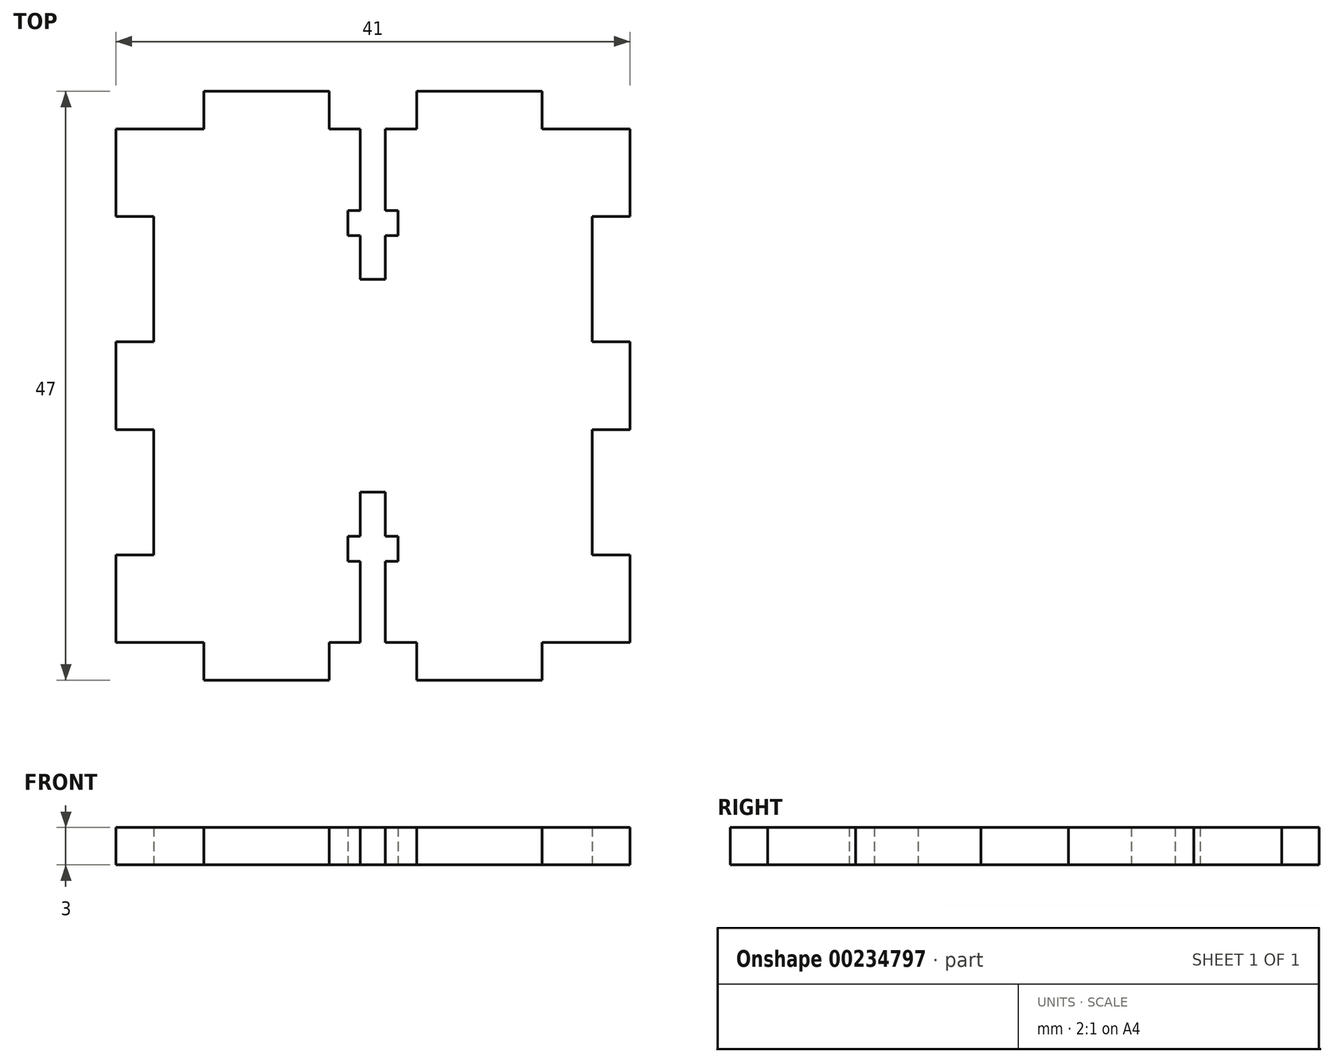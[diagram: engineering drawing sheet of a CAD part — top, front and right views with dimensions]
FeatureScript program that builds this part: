
annotation { "Feature Type Name" : "Feature", "Feature Type Description" : "" }
export const myFeature = defineFeature(function(context is Context, id is Id, definition is map)
    precondition{}
    {
        {
            var Q0;
            Q0=qCreatedBy(makeId("Top.planeOp"),FACE);
            var sketch = newSketch(context, id + "F0", { "sketchPlane" : qUnion([Q0])});
            skLineSegment(sketch, "E0.bottom", {"start": v(33.7, -13.23) * mm, "end": v(40.7, -13.23) * mm});
            skLineSegment(sketch, "E0.top", {"start": v(33.7, -54.23) * mm, "end": v(40.7, -54.23) * mm});
            skLineSegment(sketch, "E0.left", {"start": v(33.7, -13.23) * mm, "end": v(33.7, -20.23) * mm});
            skLineSegment(sketch, "E0.right", {"start": v(74.7, -13.23) * mm, "end": v(74.7, -20.23) * mm});
            skPoint(sketch, "E1", {"position": v(40.7, -13.23) * mm});
            skPoint(sketch, "E2", {"position": v(67.7, -13.23) * mm});
            skPoint(sketch, "E3", {"position": v(57.7, -13.23) * mm});
            skPoint(sketch, "E4", {"position": v(50.7, -13.23) * mm});
            skLineSegment(sketch, "E5", {"start": v(40.7, -13.23) * mm, "end": v(40.7, -10.23) * mm});
            skLineSegment(sketch, "E6", {"start": v(40.7, -10.23) * mm, "end": v(50.7, -10.23) * mm});
            skLineSegment(sketch, "E7", {"start": v(50.7, -10.23) * mm, "end": v(50.7, -13.23) * mm});
            skLineSegment(sketch, "E8", {"start": v(57.7, -13.23) * mm, "end": v(57.7, -10.23) * mm});
            skLineSegment(sketch, "E9", {"start": v(57.7, -10.23) * mm, "end": v(67.7, -10.23) * mm});
            skLineSegment(sketch, "E10", {"start": v(67.7, -10.23) * mm, "end": v(67.7, -13.23) * mm});
            skPoint(sketch, "E11", {"position": v(53.2, -13.23) * mm});
            skPoint(sketch, "E12", {"position": v(55.2, -13.23) * mm});
            skLineSegment(sketch, "E13", {"start": v(53.2, -13.23) * mm, "end": v(53.2, -19.73) * mm});
            skLineSegment(sketch, "E14", {"start": v(53.2, -19.73) * mm, "end": v(52.2, -19.73) * mm});
            skLineSegment(sketch, "E15", {"start": v(52.2, -19.73) * mm, "end": v(52.2, -21.73) * mm});
            skLineSegment(sketch, "E16", {"start": v(52.2, -21.73) * mm, "end": v(53.2, -21.73) * mm});
            skLineSegment(sketch, "E17", {"start": v(53.2, -21.73) * mm, "end": v(53.2, -25.23) * mm});
            skLineSegment(sketch, "E18", {"start": v(53.2, -25.23) * mm, "end": v(55.2, -25.23) * mm});
            skLineSegment(sketch, "E19", {"start": v(55.2, -25.23) * mm, "end": v(55.2, -21.73) * mm});
            skLineSegment(sketch, "E20", {"start": v(55.2, -21.73) * mm, "end": v(56.2, -21.73) * mm});
            skLineSegment(sketch, "E21", {"start": v(55.2, -19.73) * mm, "end": v(56.2, -19.73) * mm});
            skLineSegment(sketch, "E22", {"start": v(56.2, -19.73) * mm, "end": v(56.2, -21.73) * mm});
            skLineSegment(sketch, "E23.trimOffspring", {"start": v(55.2, -13.23) * mm, "end": v(57.7, -13.23) * mm});
            skLineSegment(sketch, "E24.trimOffspring", {"start": v(67.7, -13.23) * mm, "end": v(74.7, -13.23) * mm});
            skLineSegment(sketch, "E25.trimOffspring", {"start": v(50.7, -13.23) * mm, "end": v(53.2, -13.23) * mm});
            skLineSegment(sketch, "E26.MirrorCS", {"start": v(55.2, -45.73) * mm, "end": v(56.2, -45.73) * mm});
            skLineSegment(sketch, "E27.MirrorCS", {"start": v(52.2, -45.73) * mm, "end": v(53.2, -45.73) * mm});
            skLineSegment(sketch, "E28.MirrorCS", {"start": v(55.2, -47.73) * mm, "end": v(56.2, -47.73) * mm});
            skLineSegment(sketch, "E29.MirrorCS", {"start": v(56.2, -47.73) * mm, "end": v(56.2, -45.73) * mm});
            skLineSegment(sketch, "E30.MirrorCS", {"start": v(52.2, -47.73) * mm, "end": v(52.2, -45.73) * mm});
            skLineSegment(sketch, "E31.MirrorCS", {"start": v(53.2, -47.73) * mm, "end": v(52.2, -47.73) * mm});
            skLineSegment(sketch, "E32.MirrorCS", {"start": v(53.2, -42.23) * mm, "end": v(55.2, -42.23) * mm});
            skLineSegment(sketch, "E33.MirrorCS", {"start": v(55.2, -54.23) * mm, "end": v(57.7, -54.23) * mm});
            skLineSegment(sketch, "E34.MirrorCS", {"start": v(50.7, -57.23) * mm, "end": v(50.7, -54.23) * mm});
            skLineSegment(sketch, "E35.MirrorCS", {"start": v(57.7, -54.23) * mm, "end": v(57.7, -57.23) * mm});
            skLineSegment(sketch, "E36.MirrorCS", {"start": v(67.7, -57.23) * mm, "end": v(67.7, -54.23) * mm});
            skLineSegment(sketch, "E37.MirrorCS", {"start": v(50.7, -54.23) * mm, "end": v(53.2, -54.23) * mm});
            skLineSegment(sketch, "E38.MirrorCS", {"start": v(40.7, -54.23) * mm, "end": v(40.7, -57.23) * mm});
            skPoint(sketch, "E39.MirrorP", {"position": v(55.2, -54.23) * mm});
            skPoint(sketch, "E40.MirrorP", {"position": v(50.7, -54.23) * mm});
            skPoint(sketch, "E41.MirrorP", {"position": v(40.7, -54.23) * mm});
            skPoint(sketch, "E42.MirrorP", {"position": v(67.7, -54.23) * mm});
            skLineSegment(sketch, "E43.MirrorCS", {"start": v(57.7, -57.23) * mm, "end": v(67.7, -57.23) * mm});
            skPoint(sketch, "E44.MirrorP", {"position": v(57.7, -54.23) * mm});
            skLineSegment(sketch, "E45.MirrorCS", {"start": v(53.2, -54.23) * mm, "end": v(53.2, -47.73) * mm});
            skPoint(sketch, "E46.MirrorP", {"position": v(53.2, -54.23) * mm});
            skLineSegment(sketch, "E47.MirrorCS", {"start": v(67.7, -54.23) * mm, "end": v(74.7, -54.23) * mm});
            skLineSegment(sketch, "E48.MirrorCS", {"start": v(55.2, -42.23) * mm, "end": v(55.2, -45.73) * mm});
            skLineSegment(sketch, "E49.MirrorCS", {"start": v(53.2, -45.73) * mm, "end": v(53.2, -42.23) * mm});
            skLineSegment(sketch, "E50.MirrorCS", {"start": v(40.7, -57.23) * mm, "end": v(50.7, -57.23) * mm});
            skPoint(sketch, "E51", {"position": v(74.7, -20.23) * mm});
            skPoint(sketch, "E52", {"position": v(74.7, -47.23) * mm});
            skPoint(sketch, "E53", {"position": v(74.7, -33.73) * mm});
            skPoint(sketch, "E54", {"position": v(74.7, -30.23) * mm});
            skPoint(sketch, "E55", {"position": v(74.7, -37.23) * mm});
            skLineSegment(sketch, "E56.trimOffspring", {"start": v(74.7, -30.23) * mm, "end": v(74.7, -37.23) * mm});
            skLineSegment(sketch, "E57.trimOffspring", {"start": v(74.7, -47.23) * mm, "end": v(74.7, -54.23) * mm});
            skPoint(sketch, "E58.MirrorP", {"position": v(33.7, -37.23) * mm});
            skPoint(sketch, "E59.MirrorP", {"position": v(33.7, -47.23) * mm});
            skLineSegment(sketch, "E60.MirrorCS", {"start": v(33.7, -47.23) * mm, "end": v(33.7, -54.23) * mm});
            skPoint(sketch, "E61.MirrorP", {"position": v(33.7, -30.23) * mm});
            skPoint(sketch, "E62.MirrorP", {"position": v(33.7, -20.23) * mm});
            skPoint(sketch, "E63.MirrorP", {"position": v(33.7, -33.73) * mm});
            skLineSegment(sketch, "E64.MirrorCS", {"start": v(33.7, -30.23) * mm, "end": v(33.7, -37.23) * mm});
            skLineSegment(sketch, "E65", {"start": v(55.2, -13.23) * mm, "end": v(55.2, -19.73) * mm});
            skLineSegment(sketch, "E66", {"start": v(55.2, -54.23) * mm, "end": v(55.2, -47.73) * mm});
            skLineSegment(sketch, "E67", {"start": v(74.7, -37.23) * mm, "end": v(71.7, -37.23) * mm});
            skLineSegment(sketch, "E68", {"start": v(71.7, -37.23) * mm, "end": v(71.7, -47.23) * mm});
            skLineSegment(sketch, "E69", {"start": v(71.7, -47.23) * mm, "end": v(74.7, -47.23) * mm});
            skLineSegment(sketch, "E70", {"start": v(74.7, -30.23) * mm, "end": v(71.7, -30.23) * mm});
            skLineSegment(sketch, "E71", {"start": v(71.7, -30.23) * mm, "end": v(71.7, -20.23) * mm});
            skLineSegment(sketch, "E72", {"start": v(71.7, -20.23) * mm, "end": v(74.7, -20.23) * mm});
            skLineSegment(sketch, "E73", {"start": v(33.7, -37.23) * mm, "end": v(36.7, -37.23) * mm});
            skLineSegment(sketch, "E74", {"start": v(36.7, -37.23) * mm, "end": v(36.7, -47.23) * mm});
            skLineSegment(sketch, "E75", {"start": v(36.7, -47.23) * mm, "end": v(33.7, -47.23) * mm});
            skLineSegment(sketch, "E76", {"start": v(33.7, -30.23) * mm, "end": v(36.7, -30.23) * mm});
            skLineSegment(sketch, "E77", {"start": v(36.7, -30.23) * mm, "end": v(36.7, -20.23) * mm});
            skLineSegment(sketch, "E78", {"start": v(36.7, -20.23) * mm, "end": v(33.7, -20.23) * mm});
            skSolve(sketch);
        }
        {
            var Q0;
            Q0=makeQuery(id+"F0.imprint","IMPRINT",FACE,{"disambiguationData":[TD([[makeQuery(id+"F0.imprint","IMPRINT",EDGE,{"derivedFrom":sQuery(id+"F0.wireOp",EDGE,"E0.bottom")}),-1.0]])]});
            extrude(context, id + "F1", {"entities" : qUnion([Q0]), "endBound" : BoundingType.SYMMETRIC, "depth" : 3 * mm});
        }
    });
